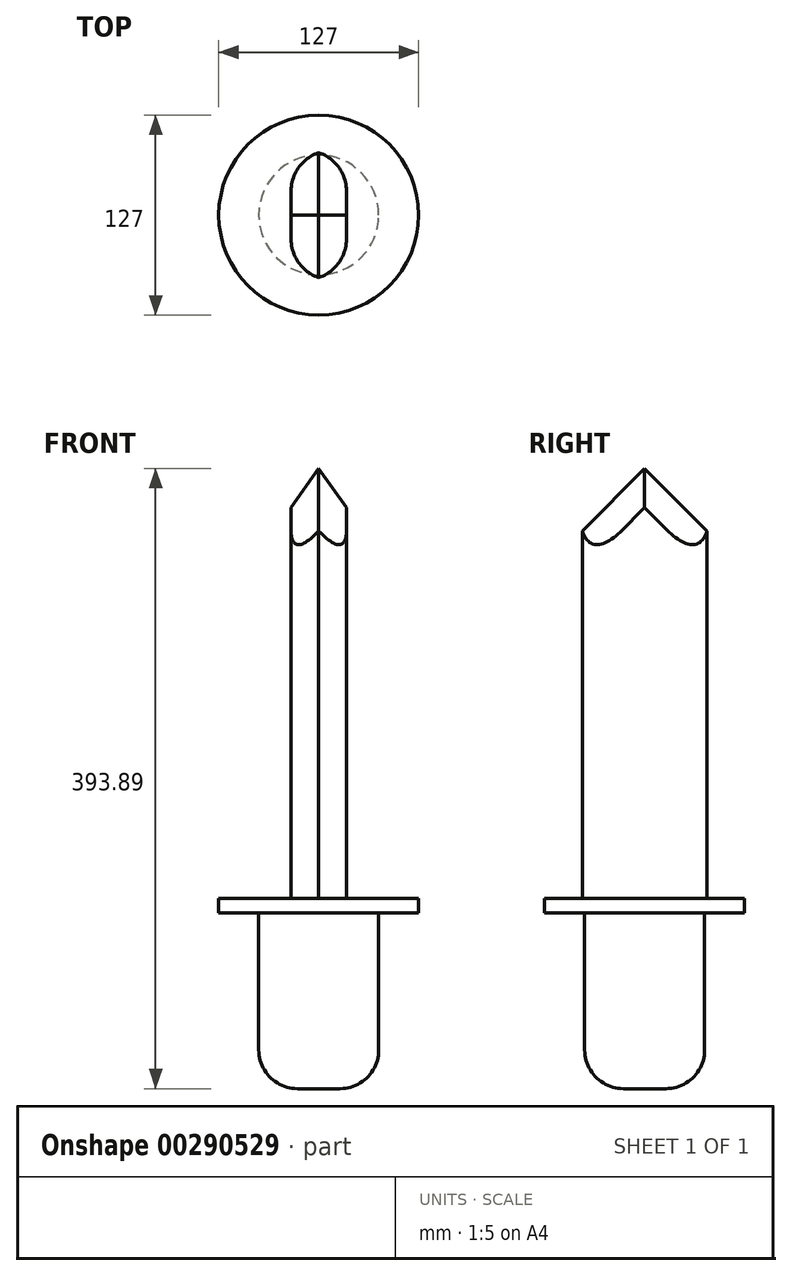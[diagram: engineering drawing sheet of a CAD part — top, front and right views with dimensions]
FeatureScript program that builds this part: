
annotation { "Feature Type Name" : "Feature", "Feature Type Description" : "" }
export const myFeature = defineFeature(function(context is Context, id is Id, definition is map)
    precondition{}
    {
        {
            var Q0;
            Q0=qCreatedBy(makeId("Top.planeOp"),FACE);
            var sketch = newSketch(context, id + "F0", { "sketchPlane" : qUnion([Q0])});
            skCircle(sketch, "E0", {"center": v(0, 0) * mm, "radius": 63.5 * mm});
            skSolve(sketch);
        }
        {
            var Q0;
            Q0=makeQuery(id+"F0.imprint","IMPRINT",FACE,{"disambiguationData":[TD([[makeQuery(id+"F0.imprint","IMPRINT",EDGE,{"derivedFrom":sQuery(id+"F0.wireOp",EDGE,"E0")}),1.0]])]});
            extrude(context, id + "F1", {"entities" : qUnion([Q0]), "depth" : 9.4 * mm});
        }
        {
            var Q0;
            Q0=makeQuery(id+"F1.opExtrude","CAP_FACE",FACE,{"disambiguationData":[OSD([sQuery(id+"F0.wireOp",EDGE,"E0")])],"isStart":true});
            var sketch = newSketch(context, id + "F2", { "sketchPlane" : qUnion([Q0])});
            skCircle(sketch, "E1", {"center": v(0, 0) * mm, "radius": 38.1 * mm});
            skSolve(sketch);
        }
        {
            var Q0;
            Q0 = qSketchRegion(id + "F2", true);
            extrude(context, id + "F3", {"entities" : qUnion([Q0]), "operationType" : NewBodyOperationType.ADD, "depth" : 111.5 * mm});
        }
        {
            var Q0;
            Q0=makeQuery(id+"F1.opExtrude","CAP_FACE",FACE,{"disambiguationData":[OSD([sQuery(id+"F0.wireOp",EDGE,"E0")])],"isStart":false});
            var sketch = newSketch(context, id + "F4", { "sketchPlane" : qUnion([Q0])});
            skLineSegment(sketch, "E2.bottom", {"start": v(17.53, 40.9) * mm, "end": v(-17.53, 40.9) * mm});
            skLineSegment(sketch, "E2.top", {"start": v(17.53, -40.9) * mm, "end": v(-17.53, -40.9) * mm});
            skLineSegment(sketch, "E2.left", {"start": v(17.53, 40.9) * mm, "end": v(17.53, -40.9) * mm});
            skLineSegment(sketch, "E2.right", {"start": v(-17.53, 40.9) * mm, "end": v(-17.53, -40.9) * mm});
            skPoint(sketch, "E2.middle", {"position": v(0, 0) * mm});
            skSolve(sketch);
        }
        {
            var Q0;
            Q0=makeQuery(id+"F4.imprint","IMPRINT",FACE,{"disambiguationData":[TD([[makeQuery(id+"F4.imprint","IMPRINT",EDGE,{"derivedFrom":sQuery(id+"F4.wireOp",EDGE,"E2.bottom")}),1.0]])]});
            extrude(context, id + "F5", {"entities" : qUnion([Q0]), "operationType" : NewBodyOperationType.ADD, "depth" : 304.8 * mm});
        }
        {
            var Q0;
            Q0=makeQuery(id+"F3.opExtrude","CAP_EDGE",EDGE,{"disambiguationData":[OSD([sQuery(id+"F2.wireOp",EDGE,"E1")])],"isStart":false});
            fillet(context, id + "F6", {"entities" : qUnion([Q0]), "radius" : 24.53 * mm, "tangentPropagation" : true, "allowEdgeOverflow" : false});
        }
        {
            var Q0;
            Q0=makeQuery(id+"F5.opExtrude","CAP_EDGE",EDGE,{"disambiguationData":[OSD([sQuery(id+"F4.wireOp",EDGE,"E2.bottom")])],"isStart":false});
            var Q1;
            Q1=makeQuery(id+"F5.opExtrude","CAP_EDGE",EDGE,{"disambiguationData":[OSD([sQuery(id+"F4.wireOp",EDGE,"E2.top")])],"isStart":false});
            chamfer(context, id + "F7", {"entities" : qUnion([Q0, Q1]), "width" : 50.8 * mm, "tangentPropagation" : true});
        }
        {
            var Q0;
            Q0=makeQuery(id+"F7.opChamfer","BLEND_EDGE",EDGE,{"blendedFrom":[makeQuery(id+"F5.opExtrude","CAP_EDGE",EDGE,{"disambiguationData":[OSD([sQuery(id+"F4.wireOp",EDGE,"E2.bottom")])],"isStart":false}),makeQuery(id+"F5.opExtrude","SWEPT_FACE",FACE,{"disambiguationData":[OSD([sQuery(id+"F4.wireOp",EDGE,"E2.left")])]})],"blendedInto":[makeQuery(id+"F5.opExtrude","SWEPT_FACE",FACE,{"disambiguationData":[OSD([sQuery(id+"F4.wireOp",EDGE,"E2.left")])]})]});
            var Q1;
            Q1=makeQuery(id+"F7.opChamfer","BLEND_EDGE",EDGE,{"blendedFrom":[makeQuery(id+"F5.opExtrude","CAP_EDGE",EDGE,{"disambiguationData":[OSD([sQuery(id+"F4.wireOp",EDGE,"E2.bottom")])],"isStart":false}),makeQuery(id+"F5.opExtrude","SWEPT_FACE",FACE,{"disambiguationData":[OSD([sQuery(id+"F4.wireOp",EDGE,"E2.right")])]})],"blendedInto":[makeQuery(id+"F5.opExtrude","SWEPT_FACE",FACE,{"disambiguationData":[OSD([sQuery(id+"F4.wireOp",EDGE,"E2.right")])]})]});
            chamfer(context, id + "F8", {"entities" : qUnion([Q0, Q1]), "width" : 33.02 * mm, "tangentPropagation" : true});
        }
        {
            var Q0;
            Q0=makeQuery(id+"F7.opChamfer","BLEND_EDGE",EDGE,{"blendedFrom":[makeQuery(id+"F5.opExtrude","CAP_EDGE",EDGE,{"disambiguationData":[OSD([sQuery(id+"F4.wireOp",EDGE,"E2.top")])],"isStart":false}),makeQuery(id+"F5.opExtrude","SWEPT_FACE",FACE,{"disambiguationData":[OSD([sQuery(id+"F4.wireOp",EDGE,"E2.right")])]})],"blendedInto":[makeQuery(id+"F5.opExtrude","SWEPT_FACE",FACE,{"disambiguationData":[OSD([sQuery(id+"F4.wireOp",EDGE,"E2.right")])]})]});
            var Q1;
            Q1=makeQuery(id+"F7.opChamfer","BLEND_EDGE",EDGE,{"blendedFrom":[makeQuery(id+"F5.opExtrude","CAP_EDGE",EDGE,{"disambiguationData":[OSD([sQuery(id+"F4.wireOp",EDGE,"E2.top")])],"isStart":false}),makeQuery(id+"F5.opExtrude","SWEPT_FACE",FACE,{"disambiguationData":[OSD([sQuery(id+"F4.wireOp",EDGE,"E2.left")])]})],"blendedInto":[makeQuery(id+"F5.opExtrude","SWEPT_FACE",FACE,{"disambiguationData":[OSD([sQuery(id+"F4.wireOp",EDGE,"E2.left")])]})]});
            chamfer(context, id + "F9", {"entities" : qUnion([Q0, Q1]), "width" : 33.02 * mm, "tangentPropagation" : true});
        }
        {
            var Q0;
            Q0=makeQuery(id+"F5.opExtrude","SWEPT_EDGE",EDGE,{"disambiguationData":[OSD([sQuery(id+"F4.wireOp",EDGE,"E2.bottom"),sQuery(id+"F4.wireOp",EDGE,"E2.right")])]});
            var Q1;
            Q1=makeQuery(id+"F5.opExtrude","SWEPT_EDGE",EDGE,{"disambiguationData":[OSD([sQuery(id+"F4.wireOp",EDGE,"E2.bottom"),sQuery(id+"F4.wireOp",EDGE,"E2.left")])]});
            var Q2;
            Q2=makeQuery(id+"F5.opExtrude","SWEPT_EDGE",EDGE,{"disambiguationData":[OSD([sQuery(id+"F4.wireOp",EDGE,"E2.top"),sQuery(id+"F4.wireOp",EDGE,"E2.right")])]});
            var Q3;
            Q3=makeQuery(id+"F5.opExtrude","SWEPT_EDGE",EDGE,{"disambiguationData":[OSD([sQuery(id+"F4.wireOp",EDGE,"E2.top"),sQuery(id+"F4.wireOp",EDGE,"E2.left")])]});
            fillet(context, id + "F10", {"entities" : qUnion([Q0, Q1, Q2, Q3]), "radius" : 25.4 * mm, "tangentPropagation" : true, "allowEdgeOverflow" : false});
        }
    });
